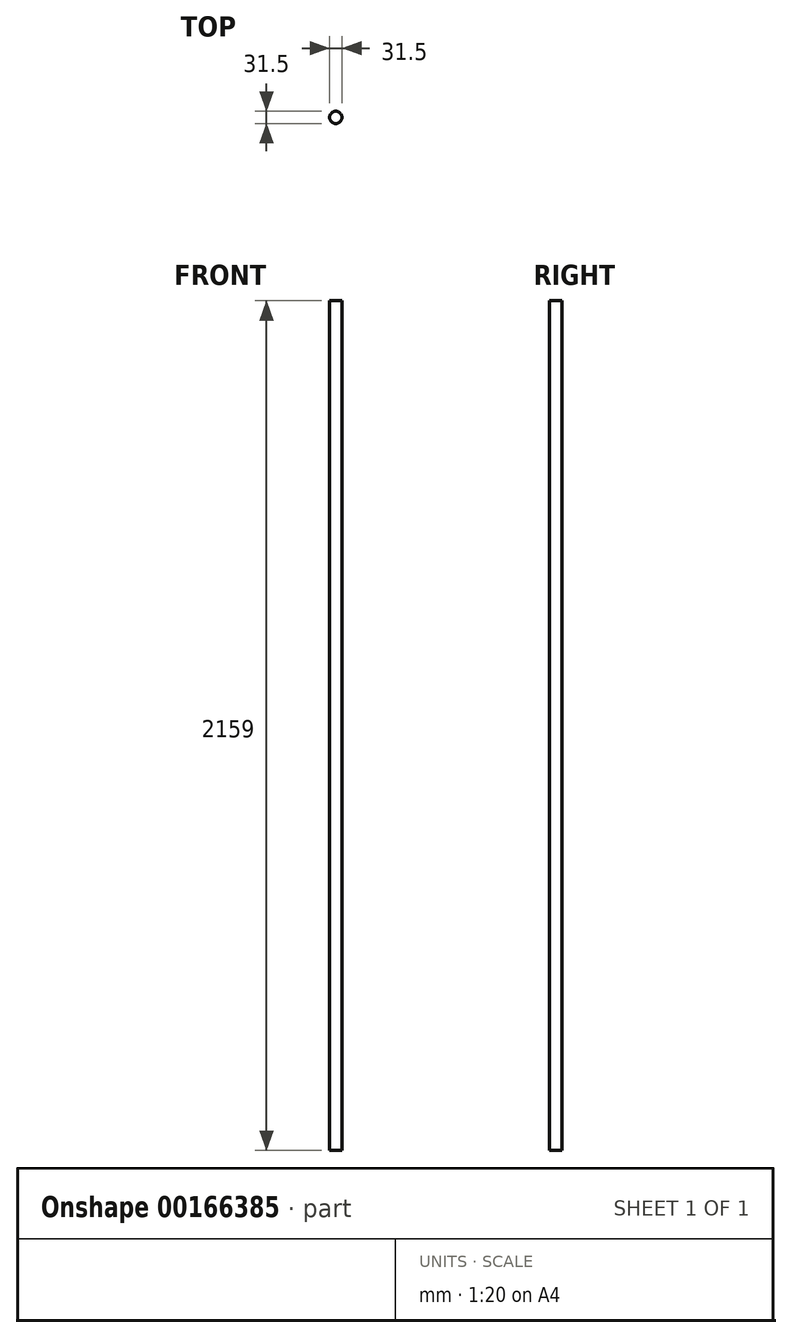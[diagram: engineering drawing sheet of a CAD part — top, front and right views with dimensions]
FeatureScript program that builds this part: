
annotation { "Feature Type Name" : "Feature", "Feature Type Description" : "" }
export const myFeature = defineFeature(function(context is Context, id is Id, definition is map)
    precondition{}
    {
        {
            var Q0;
            Q0=qCreatedBy(makeId("Top.planeOp"),FACE);
            var sketch = newSketch(context, id + "F0", { "sketchPlane" : qUnion([Q0])});
            skCircle(sketch, "E0", {"center": v(0, 0) * mm, "radius": 15.75 * mm});
            skSolve(sketch);
        }
        {
            var Q0;
            Q0=makeQuery(id+"F0.imprint","IMPRINT",FACE,{"disambiguationData":[TD([[makeQuery(id+"F0.imprint","IMPRINT",EDGE,{"derivedFrom":sQuery(id+"F0.wireOp",EDGE,"E0")}),1.0]])]});
            extrude(context, id + "F1", {"entities" : qUnion([Q0]), "depth" : 2159 * mm});
        }
    });
